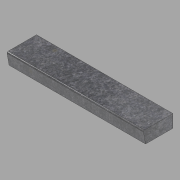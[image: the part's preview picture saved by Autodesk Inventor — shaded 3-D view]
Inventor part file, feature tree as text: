
AUTODESK INVENTOR PART (.ipt)
format: ipt  version: 2022.1 (Build 261234020, 234B)  size: 98,304 bytes
history: native  units: in
note: dims shown in document units (in); Inventor stores cm internally (conversion verified against a paired STEP export)
features: other x3, extrude x1, sketch x1
ambient origin geometry x8: Origin, YZ Plane, XZ Plane, XY Plane, X Axis, Y Axis, Z Axis, Center Point
bodies: Solid1 (feature_tree)
feature tree (5):
  other  "Blocks"
  extrude  "Extrusion1"  Depth=64.75in TaperAngle=0.0deg
  sketch  "Sketch1"  dims[d0=13.0in d1=6.0in d2=13.5in d3=0.5in d4=0.5in d5=64.75in d6=0.0in]
  other  "Profile"
  other  "Profile:1"
